# Revit family: LOROWERK 00600-EF0X
name_source: partatom
category: Rohrformteile
revit_build: Autodesk Revit 2017 (Build: 20160225_1515(x64)
units: mm (PartAtom-declared; Revit-internal decimal feet)

## family parameters
Arbeitsebenenbasiert = Nein
Beim Laden mit Abzugskörper schneiden = Nein
Bemaßung runder Anschluss = Durchmesser verwenden
Gemeinsam genutzt = Nein
Immer vertikal = Ja
Teiletyp = Verbindung

## types (1)
- LOROWERK 00600-EF0X
    BIM = https://media.stage.bim.site
    Benennung = LORO-X Übergangsrohr konzentrisch, DN125/150
    Beschreibung = LORO-X Stahlabflussrohre
    Bestellmenge (Multiplikator) = 1
    Brandschutzklasse = B1 nach DIN 4102
    CONNECTOR0_DIAMETER_dZ_0r = 125 mm
    CONNECTOR0_dZ_00 = 145 mm
    CONNECTOR0_dZ_01 = 225 mm  [stored 0.738189 ft]
    CONNECTOR0_ref_dZ = 145 mm
    CONNECTOR1_DIAMETER_dZ_0r = 150 mm
    CONNECTOR1_dZ_01 = 85 mm
    CONNECTOR1_ref_dZ = 85 mm
    DATANORM = 00600.EF0X
    GTIN = 4038088027318
    HAN = 00600.EF0X
    Hersteller = LOROWERK K.H. Vahlbrauk GmbH & Co. KG
    Index = 10
    Ist System = Nein
    Ist Zubehör = Nein
    Nenndruck = 0.5
    Nenndrucksystem = PN
    Nennweitensystem = DN
    Normen/Regeln/Zulassungen = DVGW für Trinkwasser
    Produktbezeichnung = LORO-X Stahlabflussrohre
    Produktkennung = Formstück
    Produktname = Anschlussstücke von LORO-X Rohr an Kunststoffabflussrohrmuffen (KA)
    Produktvideo = https://media.stage.bim.site
    Querschnittsform = rund
    Typname = Anschlussstücke von LORO-X Rohr an Kunststoffabflussrohrmuffen (KA)
    VDIBSN = 020001???001001???00100100000100300700000000000170000000000000000010
    Verbindungsart I = Pressen
    Verbindungsart II = axial pressen
    Verlegeart = unter Putz
    max. zul. Dauer-Betriebstemperatur [Kelvin] = 95

note: [stored X ft] marks values corroborated as IEEE doubles in the binary element streams (Revit-internal decimal feet)
